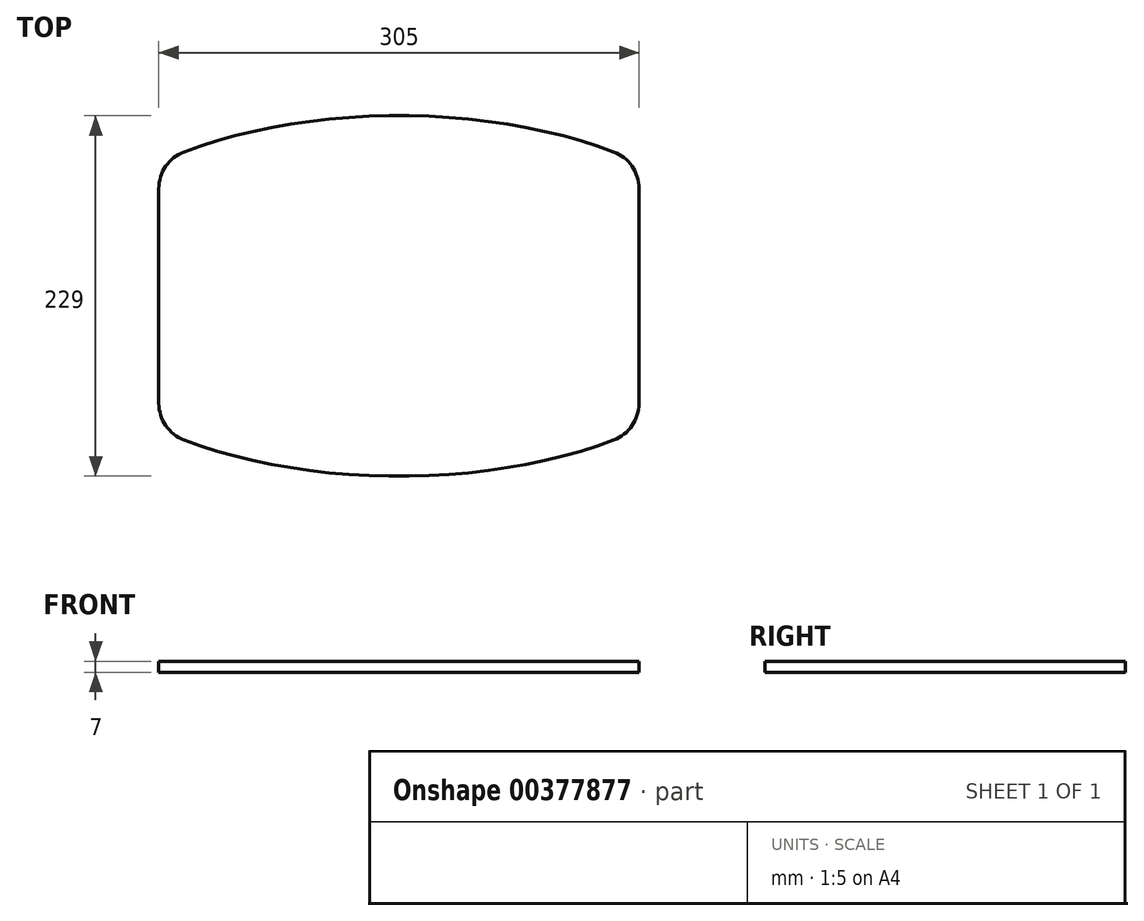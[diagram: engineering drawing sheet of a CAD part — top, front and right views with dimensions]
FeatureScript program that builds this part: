
annotation { "Feature Type Name" : "Feature", "Feature Type Description" : "" }
export const myFeature = defineFeature(function(context is Context, id is Id, definition is map)
    precondition{}
    {
        {
            var Q0;
            Q0=qCreatedBy(makeId("Top.planeOp"),FACE);
            var sketch = newSketch(context, id + "F0", { "sketchPlane" : qUnion([Q0])});
            skLineSegment(sketch, "E0.left", {"start": v(152.5, -68.17) * mm, "end": v(152.5, 68.17) * mm});
            skLineSegment(sketch, "E0.right", {"start": v(-152.5, -68.17) * mm, "end": v(-152.5, 68.17) * mm});
            skPoint(sketch, "E0.middle", {"position": v(0, 0) * mm});
            skEllipticalArc(sketch, "E1", {});
            skEllipticalArc(sketch, "E2.trimOffspring", {});
            skPoint(sketch, "E3.orphan", {"position": v(152.5, 114.5) * mm});
            skPoint(sketch, "E4.orphan", {"position": v(-152.5, 114.5) * mm});
            skPoint(sketch, "E5.orphan", {"position": v(-152.5, -114.5) * mm});
            skPoint(sketch, "E6.orphan", {"position": v(152.5, -114.5) * mm});
            skPoint(sketch, "E7.visualSharp", {"position": v(-152.5, 84.82) * mm});
            skArc(sketch, "E7.filletArc", {"start": v(-136.36, 91.55) * mm, "mid": v(-148.07, 82.37) * mm, "end": v(-152.5, 68.17) * mm});
            skPoint(sketch, "E8.visualSharp", {"position": v(152.5, 84.82) * mm});
            skArc(sketch, "E8.filletArc", {"start": v(152.5, 68.17) * mm, "mid": v(148.07, 82.37) * mm, "end": v(136.36, 91.55) * mm});
            skPoint(sketch, "E9.visualSharp", {"position": v(152.5, -84.82) * mm});
            skArc(sketch, "E9.filletArc", {"start": v(136.36, -91.55) * mm, "mid": v(148.07, -82.37) * mm, "end": v(152.5, -68.17) * mm});
            skPoint(sketch, "E10.visualSharp", {"position": v(-152.5, -84.82) * mm});
            skArc(sketch, "E10.filletArc", {"start": v(-152.5, -68.17) * mm, "mid": v(-148.07, -82.37) * mm, "end": v(-136.36, -91.55) * mm});
            const initialGuessF0  = {"E1": [0, 0, 1, 0, 0.2270268201828003, 0.1145, 4.068109515696408, 5.356668445192201], "E2.trimOffspring": [0, 0, 1, 0, 0.2270268201828003, 0.1145, 0.9265168619873848, 2.215075791602408]};
            skSetInitialGuess(sketch, initialGuessF0);
            skSolve(sketch);
        }
        {
            var Q0;
            Q0=makeQuery(id+"F0.imprint","IMPRINT",FACE,{"disambiguationData":[TD([[makeQuery(id+"F0.imprint","IMPRINT",EDGE,{"derivedFrom":sQuery(id+"F0.wireOp",EDGE,"E0.left")}),1.0]])]});
            extrude(context, id + "F1", {"entities" : qUnion([Q0]), "depth" : 7 * mm});
        }
    });
